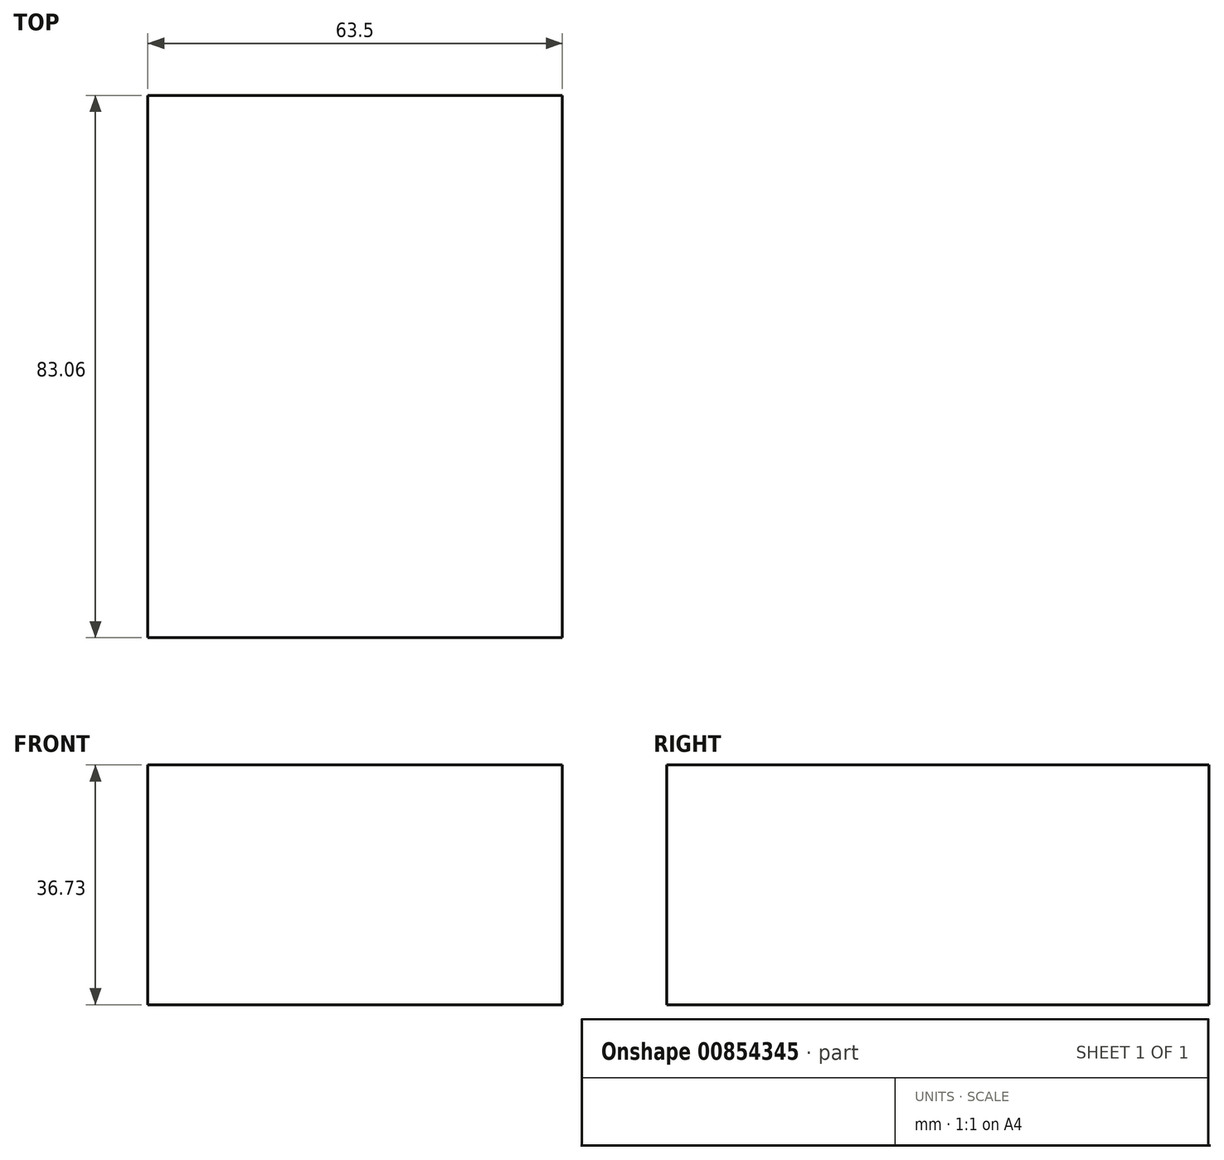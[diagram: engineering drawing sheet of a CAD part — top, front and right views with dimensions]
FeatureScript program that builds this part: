
annotation { "Feature Type Name" : "Feature", "Feature Type Description" : "" }
export const myFeature = defineFeature(function(context is Context, id is Id, definition is map)
    precondition{}
    {
        {
            var Q0;
            Q0=qCreatedBy(makeId("Front.planeOp"),FACE);
            var sketch = newSketch(context, id + "F0", { "sketchPlane" : qUnion([Q0])});
            skLineSegment(sketch, "E0.bottom", {"start": v(31.75, 16.26) * mm, "end": v(-31.75, 16.26) * mm});
            skLineSegment(sketch, "E0.top", {"start": v(31.75, -20.47) * mm, "end": v(-31.75, -20.47) * mm});
            skLineSegment(sketch, "E0.left", {"start": v(31.75, 16.26) * mm, "end": v(31.75, -20.47) * mm});
            skLineSegment(sketch, "E0.right", {"start": v(-31.75, 16.26) * mm, "end": v(-31.75, -20.47) * mm});
            skPoint(sketch, "E0.middle", {"position": v(0, -2.1) * mm});
            skLineSegment(sketch, "E1.bottom", {"start": v(86.22, 50.3) * mm, "end": v(48.12, 50.3) * mm});
            skLineSegment(sketch, "E1.top", {"start": v(86.22, 24.9) * mm, "end": v(48.12, 24.9) * mm});
            skLineSegment(sketch, "E1.left", {"start": v(86.22, 50.3) * mm, "end": v(86.22, 24.9) * mm});
            skLineSegment(sketch, "E1.right", {"start": v(48.12, 50.3) * mm, "end": v(48.12, 24.9) * mm});
            skPoint(sketch, "E1.middle", {"position": v(67.17, 37.6) * mm});
            skLineSegment(sketch, "E2", {"start": v(31.75, 16.26) * mm, "end": v(31.75, 24.45) * mm});
            skArc(sketch, "E3", {"start": v(31.75, 24.45) * mm, "mid": v(33.87, 28.98) * mm, "end": v(38.71, 30.25) * mm});
            skLineSegment(sketch, "E4", {"start": v(38.71, 30.25) * mm, "end": v(67.31, 30.25) * mm});
            skSolve(sketch);
        }
        {
            var Q0;
            Q0=qCreatedBy(makeId("Right.planeOp"),FACE);
            var sketch = newSketch(context, id + "F1", { "sketchPlane" : qUnion([Q0])});
            skLineSegment(sketch, "E5.0", {"start": v(6.35, 16.26) * mm, "end": v(6.35, 24.45) * mm});
            skSolve(sketch);
        }
        {
            var Q0;
            Q0 = qSketchRegion(id + "F1", true);
            var Q1;
            Q1=makeQuery(id+"F0.imprint","IMPRINT",FACE,{"disambiguationData":[TD([[makeQuery(id+"F0.imprint","IMPRINT",EDGE,{"derivedFrom":sQuery(id+"F0.wireOp",EDGE,"E0.bottom")}),1.0]])]});
            extrude(context, id + "F2", {"entities" : qUnion([Q0, Q1]), "oppositeDirection" : true, "depth" : 83.06 * mm, "offsetDistance" : 25.4 * mm});
        }
    });
